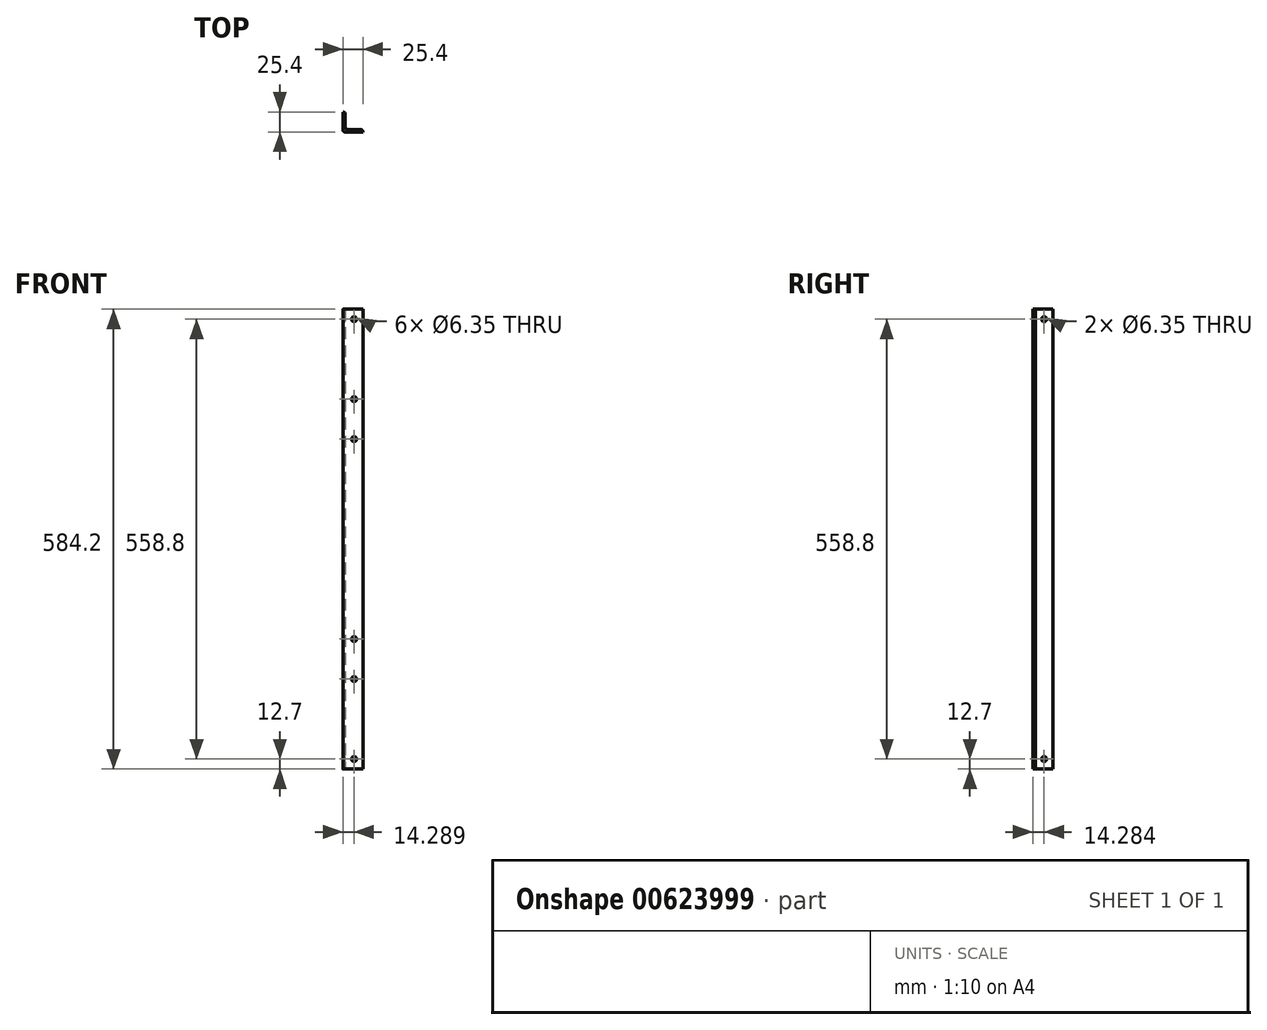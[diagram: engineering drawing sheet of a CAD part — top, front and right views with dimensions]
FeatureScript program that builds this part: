
annotation { "Feature Type Name" : "Feature", "Feature Type Description" : "" }
export const myFeature = defineFeature(function(context is Context, id is Id, definition is map)
    precondition{}
    {
        {
            var Q0;
            Q0=qCreatedBy(makeId("Top.planeOp"),FACE);
            var sketch = newSketch(context, id + "F0", { "sketchPlane" : qUnion([Q0])});
            skLineSegment(sketch, "E0", {"start": v(-21.86, 6.62) * mm, "end": v(-21.86, -18.78) * mm});
            skLineSegment(sketch, "E1", {"start": v(-21.86, -18.78) * mm, "end": v(3.54, -18.78) * mm});
            skLineSegment(sketch, "E2", {"start": v(3.54, -18.78) * mm, "end": v(3.54, -15.6) * mm});
            skLineSegment(sketch, "E3", {"start": v(3.54, -15.6) * mm, "end": v(-18.68, -15.6) * mm});
            skLineSegment(sketch, "E4", {"start": v(-18.68, -15.6) * mm, "end": v(-18.68, 6.62) * mm});
            skLineSegment(sketch, "E5", {"start": v(-18.68, 6.62) * mm, "end": v(-21.86, 6.62) * mm});
            skSolve(sketch);
        }
        {
            var Q0;
            Q0=makeQuery(id+"F0.imprint","IMPRINT",FACE,{"disambiguationData":[TD([[makeQuery(id+"F0.imprint","IMPRINT",EDGE,{"derivedFrom":sQuery(id+"F0.wireOp",EDGE,"E0")}),1.0]])]});
            extrude(context, id + "F1", {"entities" : qUnion([Q0]), "depth" : 584.2 * mm, "offsetDistance" : 25.4 * mm});
        }
        {
            var Q0;
            Q0=makeQuery(id+"F1.opExtrude","SWEPT_FACE",FACE,{"disambiguationData":[OSD([sQuery(id+"F0.wireOp",EDGE,"E4")])]});
            var sketch = newSketch(context, id + "F2", { "sketchPlane" : qUnion([Q0])});
            skCircle(sketch, "E6", {"center": v(-4.5, 12.7) * mm, "radius": 3.18 * mm});
            skPoint(sketch, "E6.centerSnap0", {"position": v(-4.5, 0) * mm});
            skCircle(sketch, "E7", {"center": v(-4.5, 571.5) * mm, "radius": 3.18 * mm});
            skPoint(sketch, "E7.centerSnap0", {"position": v(-4.5, 584.2) * mm});
            skSolve(sketch);
        }
        {
            var Q0;
            Q0=makeQuery(id+"F2.imprint","IMPRINT",FACE,{"disambiguationData":[TD([[makeQuery(id+"F2.imprint","IMPRINT",EDGE,{"derivedFrom":sQuery(id+"F2.wireOp",EDGE,"E7")}),1.0]])]});
            var Q1;
            Q1=makeQuery(id+"F2.imprint","IMPRINT",FACE,{"disambiguationData":[TD([[makeQuery(id+"F2.imprint","IMPRINT",EDGE,{"derivedFrom":sQuery(id+"F2.wireOp",EDGE,"E6")}),1.0]])]});
            extrude(context, id + "F3", {"entities" : qUnion([Q0, Q1]), "operationType" : NewBodyOperationType.REMOVE, "oppositeDirection" : true, "depth" : 3.17 * mm, "offsetDistance" : 25.4 * mm});
        }
        {
            var Q0;
            Q0=makeQuery(id+"F1.opExtrude","SWEPT_FACE",FACE,{"disambiguationData":[OSD([sQuery(id+"F0.wireOp",EDGE,"E3")])]});
            var sketch = newSketch(context, id + "F4", { "sketchPlane" : qUnion([Q0])});
            skCircle(sketch, "E8", {"center": v(7.57, 571.5) * mm, "radius": 3.18 * mm});
            skPoint(sketch, "E8.centerSnap0", {"position": v(7.57, 584.2) * mm});
            skCircle(sketch, "E9", {"center": v(7.57, 12.7) * mm, "radius": 3.18 * mm});
            skPoint(sketch, "E9.centerSnap0", {"position": v(7.57, 0) * mm});
            skSolve(sketch);
        }
        {
            var Q0;
            Q0=makeQuery(id+"F4.imprint","IMPRINT",FACE,{"disambiguationData":[TD([[makeQuery(id+"F4.imprint","IMPRINT",EDGE,{"derivedFrom":sQuery(id+"F4.wireOp",EDGE,"E9")}),1.0]])]});
            var Q1;
            Q1=makeQuery(id+"F4.imprint","IMPRINT",FACE,{"disambiguationData":[TD([[makeQuery(id+"F4.imprint","IMPRINT",EDGE,{"derivedFrom":sQuery(id+"F4.wireOp",EDGE,"E8")}),1.0]])]});
            extrude(context, id + "F5", {"entities" : qUnion([Q0, Q1]), "operationType" : NewBodyOperationType.REMOVE, "oppositeDirection" : true, "depth" : 25.4 * mm, "offsetDistance" : 25.4 * mm});
        }
        {
            var Q0;
            Q0=makeQuery(id+"F1.opExtrude","SWEPT_EDGE",EDGE,{"disambiguationData":[OSD([sQuery(id+"F0.wireOp",EDGE,"E2"),sQuery(id+"F0.wireOp",EDGE,"E3")])]});
            var Q1;
            Q1=makeQuery(id+"F1.opExtrude","SWEPT_EDGE",EDGE,{"disambiguationData":[OSD([sQuery(id+"F0.wireOp",EDGE,"E4"),sQuery(id+"F0.wireOp",EDGE,"E5")])]});
            fillet(context, id + "F6", {"entities" : qUnion([Q0, Q1]), "radius" : 3.17 * mm, "tangentPropagation" : true, "rho" : 0.5, "crossSection" : FilletCrossSection.CONIC, "allowEdgeOverflow" : false});
        }
        {
            var Q0;
            Q0=makeQuery(id+"F1.opExtrude","SWEPT_EDGE",EDGE,{"disambiguationData":[OSD([sQuery(id+"F0.wireOp",EDGE,"E0"),sQuery(id+"F0.wireOp",EDGE,"E1")])]});
            var Q1;
            Q1=makeQuery(id+"F1.opExtrude","SWEPT_EDGE",EDGE,{"disambiguationData":[OSD([sQuery(id+"F0.wireOp",EDGE,"E3"),sQuery(id+"F0.wireOp",EDGE,"E4")])]});
            fillet(context, id + "F7", {"entities" : qUnion([Q0, Q1]), "radius" : 3.17 * mm, "tangentPropagation" : true, "rho" : 0.5, "crossSection" : FilletCrossSection.CONIC, "allowEdgeOverflow" : false});
        }
        {
            var Q0;
            Q0=makeQuery(id+"F1.opExtrude","SWEPT_FACE",FACE,{"disambiguationData":[OSD([sQuery(id+"F0.wireOp",EDGE,"E3")])]});
            var sketch = newSketch(context, id + "F8", { "sketchPlane" : qUnion([Q0])});
            skCircle(sketch, "E10", {"center": v(7.57, 469.9) * mm, "radius": 3.18 * mm});
            skCircle(sketch, "E11", {"center": v(7.57, 419.1) * mm, "radius": 3.18 * mm});
            skCircle(sketch, "E12", {"center": v(7.57, 114.3) * mm, "radius": 3.18 * mm});
            skCircle(sketch, "E13", {"center": v(7.57, 165.1) * mm, "radius": 3.18 * mm});
            skSolve(sketch);
        }
        {
            var Q0;
            Q0=makeQuery(id+"F8.imprint","IMPRINT",FACE,{"disambiguationData":[TD([[makeQuery(id+"F8.imprint","IMPRINT",EDGE,{"derivedFrom":sQuery(id+"F8.wireOp",EDGE,"E13")}),1.0]])]});
            var Q1;
            Q1=makeQuery(id+"F8.imprint","IMPRINT",FACE,{"disambiguationData":[TD([[makeQuery(id+"F8.imprint","IMPRINT",EDGE,{"derivedFrom":sQuery(id+"F8.wireOp",EDGE,"E12")}),1.0]])]});
            var Q2;
            Q2=makeQuery(id+"F8.imprint","IMPRINT",FACE,{"disambiguationData":[TD([[makeQuery(id+"F8.imprint","IMPRINT",EDGE,{"derivedFrom":sQuery(id+"F8.wireOp",EDGE,"E10")}),1.0]])]});
            var Q3;
            Q3=makeQuery(id+"F8.imprint","IMPRINT",FACE,{"disambiguationData":[TD([[makeQuery(id+"F8.imprint","IMPRINT",EDGE,{"derivedFrom":sQuery(id+"F8.wireOp",EDGE,"E11")}),1.0]])]});
            extrude(context, id + "F9", {"entities" : qUnion([Q0, Q1, Q2, Q3]), "operationType" : NewBodyOperationType.REMOVE, "oppositeDirection" : true, "depth" : 3.17 * mm, "offsetDistance" : 25.4 * mm});
        }
    });
